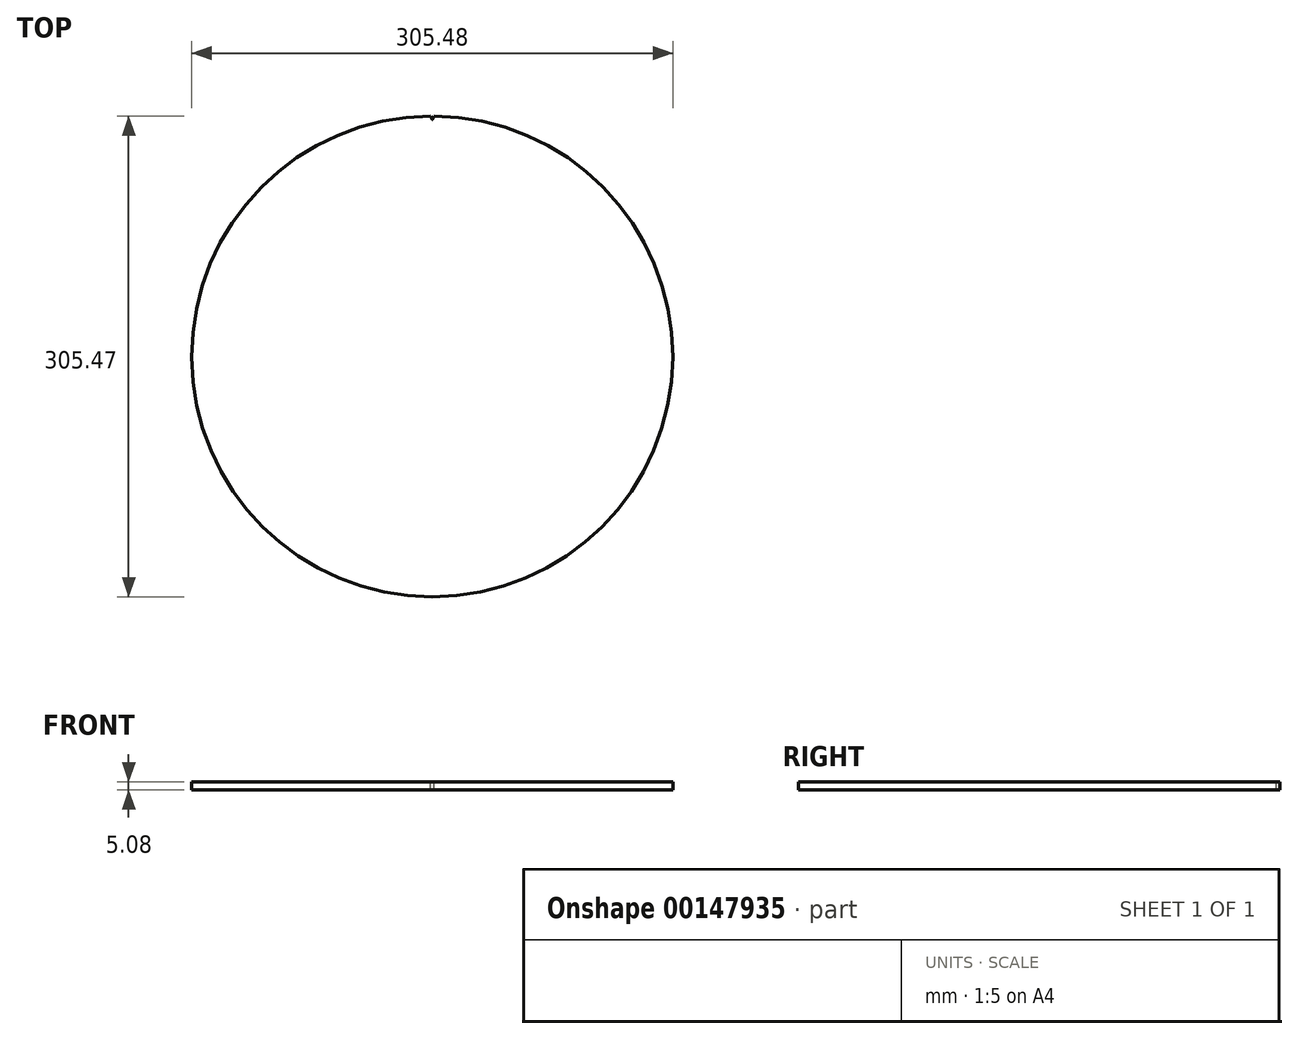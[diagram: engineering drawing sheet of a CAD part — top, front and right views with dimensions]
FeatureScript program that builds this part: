
annotation { "Feature Type Name" : "Feature", "Feature Type Description" : "" }
export const myFeature = defineFeature(function(context is Context, id is Id, definition is map)
    precondition{}
    {
        {
            var Q0;
            Q0=qCreatedBy(makeId("Top.planeOp"),FACE);
            var sketch = newSketch(context, id + "F0", { "sketchPlane" : qUnion([Q0])});
            skCircle(sketch, "E0", {"center": v(0, 0) * mm, "radius": 152.74 * mm});
            skSolve(sketch);
        }
        {
            var Q0;
            Q0=qSketchRegion(id+"F0",true);
            extrude(context, id + "F1", {"entities" : qUnion([Q0]), "depth" : 5.08 * mm});
        }
        {
            var Q0;
            Q0=makeQuery(id+"F1.opExtrude","CAP_FACE",FACE,{"disambiguationData":[OSD([sQuery(id+"F0.wireOp",EDGE,"E0")])],"isStart":false});
            var sketch = newSketch(context, id + "F2", { "sketchPlane" : qUnion([Q0])});
            skLineSegment(sketch, "E1", {"start": v(0, 0) * mm, "end": v(0, 152.74) * mm, "construction": true});
            skLineSegment(sketch, "E2", {"start": v(0, 0) * mm, "end": v(0.65, 152.74) * mm, "construction": true});
            skArc(sketch, "E3", {"start": v(1, 152.73) * mm, "mid": v(0, 152.74) * mm, "end": v(-1, 152.73) * mm});
            skLineSegment(sketch, "E4", {"start": v(-1, 152.73) * mm, "end": v(-0.28, 150.76) * mm});
            skLineSegment(sketch, "E5", {"start": v(1, 152.73) * mm, "end": v(0.28, 150.76) * mm});
            skArc(sketch, "E6", {"start": v(-0.28, 150.76) * mm, "mid": v(0, 150.56) * mm, "end": v(0.28, 150.76) * mm});
            skPoint(sketch, "E7", {"position": v(0.64, 151.75) * mm});
            skSolve(sketch);
        }
        {
            var Q0;
            Q0=qSketchRegion(id+"F2",true);
            var Q1;
            Q1=makeQuery(id+"F1.opExtrude","CAP_FACE",FACE,{"disambiguationData":[OSD([sQuery(id+"F0.wireOp",EDGE,"E0")])],"isStart":true});
            extrude(context, id + "F3", {"entities" : qUnion([Q0]), "operationType" : NewBodyOperationType.REMOVE, "endBound" : BoundingType.UP_TO_SURFACE, "oppositeDirection" : true, "endBoundEntityFace" : qUnion([Q1]), "depth" : 25.4 * mm});
        }
    });
